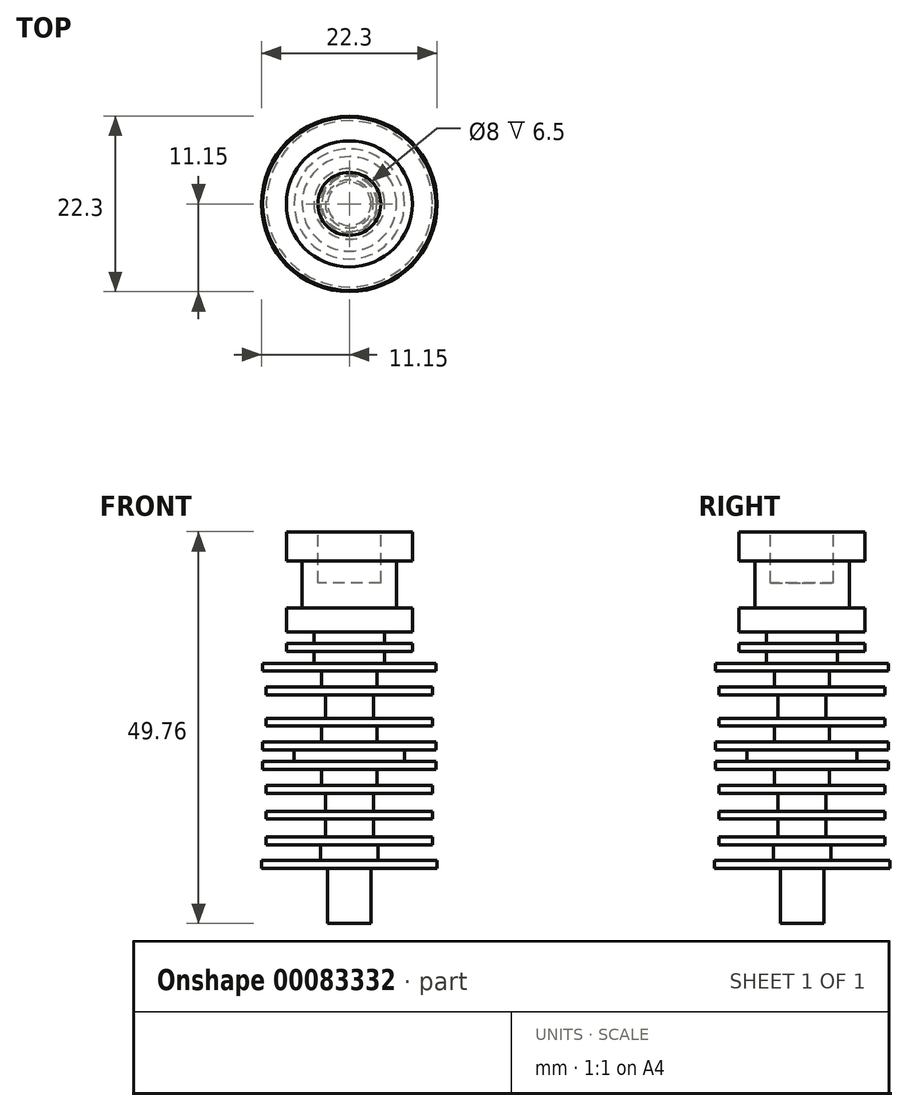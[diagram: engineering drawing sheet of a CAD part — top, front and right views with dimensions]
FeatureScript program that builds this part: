
annotation { "Feature Type Name" : "Feature", "Feature Type Description" : "" }
export const myFeature = defineFeature(function(context is Context, id is Id, definition is map)
    precondition{}
    {
        {
            var Q0;
            Q0=qCreatedBy(makeId("Front.planeOp"),FACE);
            var sketch = newSketch(context, id + "F0", { "sketchPlane" : qUnion([Q0])});
            skLineSegment(sketch, "E0", {"start": v(2.75, 0) * mm, "end": v(11.15, 0) * mm});
            skLineSegment(sketch, "E1", {"start": v(11.15, 0) * mm, "end": v(11.15, 1) * mm});
            skLineSegment(sketch, "E2", {"start": v(11.15, 1) * mm, "end": v(3.65, 1) * mm});
            skLineSegment(sketch, "E3", {"start": v(3.65, 1) * mm, "end": v(3.65, 3) * mm});
            skLineSegment(sketch, "E4", {"start": v(3.65, 3) * mm, "end": v(10.55, 3) * mm});
            skLineSegment(sketch, "E5", {"start": v(10.55, 3) * mm, "end": v(10.55, 4) * mm});
            skLineSegment(sketch, "E6", {"start": v(10.55, 4) * mm, "end": v(3.05, 4) * mm});
            skLineSegment(sketch, "E7", {"start": v(3.05, 4) * mm, "end": v(3.05, 6.25) * mm});
            skLineSegment(sketch, "E8", {"start": v(3.05, 6.25) * mm, "end": v(10.55, 6.25) * mm});
            skLineSegment(sketch, "E9", {"start": v(10.55, 6.25) * mm, "end": v(10.55, 7.25) * mm});
            skLineSegment(sketch, "E10", {"start": v(10.55, 7.25) * mm, "end": v(3.05, 7.25) * mm});
            skLineSegment(sketch, "E11", {"start": v(3.05, 7.25) * mm, "end": v(3.05, 9.5) * mm});
            skLineSegment(sketch, "E12", {"start": v(3.05, 9.5) * mm, "end": v(10.55, 9.5) * mm});
            skLineSegment(sketch, "E13", {"start": v(10.55, 9.5) * mm, "end": v(10.55, 10.56) * mm});
            skLineSegment(sketch, "E14", {"start": v(10.55, 10.56) * mm, "end": v(3.5, 10.56) * mm});
            skLineSegment(sketch, "E15", {"start": v(3.5, 10.56) * mm, "end": v(3.5, 12.56) * mm});
            skLineSegment(sketch, "E16", {"start": v(3.5, 12.56) * mm, "end": v(11, 12.56) * mm});
            skLineSegment(sketch, "E17", {"start": v(11, 12.56) * mm, "end": v(11, 13.56) * mm});
            skLineSegment(sketch, "E18", {"start": v(11, 13.56) * mm, "end": v(7, 13.56) * mm});
            skLineSegment(sketch, "E19", {"start": v(7, 13.56) * mm, "end": v(7, 15.06) * mm});
            skLineSegment(sketch, "E20", {"start": v(7, 15.06) * mm, "end": v(11, 15.06) * mm});
            skLineSegment(sketch, "E21", {"start": v(11, 15.06) * mm, "end": v(11, 16.06) * mm});
            skLineSegment(sketch, "E22", {"start": v(11, 16.06) * mm, "end": v(3.5, 16.06) * mm});
            skLineSegment(sketch, "E23", {"start": v(3.5, 16.06) * mm, "end": v(3.5, 18.06) * mm});
            skLineSegment(sketch, "E24", {"start": v(3.5, 18.06) * mm, "end": v(10.55, 18.06) * mm});
            skLineSegment(sketch, "E25", {"start": v(10.55, 18.06) * mm, "end": v(10.55, 19.06) * mm});
            skLineSegment(sketch, "E26", {"start": v(10.55, 19.06) * mm, "end": v(3.05, 19.06) * mm});
            skLineSegment(sketch, "E27", {"start": v(3.05, 19.06) * mm, "end": v(3.05, 22.06) * mm});
            skLineSegment(sketch, "E28", {"start": v(3.05, 22.06) * mm, "end": v(10.55, 22.06) * mm});
            skLineSegment(sketch, "E29", {"start": v(10.55, 22.06) * mm, "end": v(10.55, 23.06) * mm});
            skLineSegment(sketch, "E30", {"start": v(10.55, 23.06) * mm, "end": v(3.5, 23.06) * mm});
            skLineSegment(sketch, "E31", {"start": v(3.5, 23.06) * mm, "end": v(3.5, 25.06) * mm});
            skLineSegment(sketch, "E32", {"start": v(3.5, 25.06) * mm, "end": v(11, 25.06) * mm});
            skLineSegment(sketch, "E33", {"start": v(11, 25.06) * mm, "end": v(11, 26.06) * mm});
            skLineSegment(sketch, "E34", {"start": v(11, 26.06) * mm, "end": v(4.5, 26.06) * mm});
            skLineSegment(sketch, "E35", {"start": v(4.5, 26.06) * mm, "end": v(4.5, 27.56) * mm});
            skLineSegment(sketch, "E36", {"start": v(4.5, 27.56) * mm, "end": v(8, 27.56) * mm});
            skLineSegment(sketch, "E37", {"start": v(8, 27.56) * mm, "end": v(8, 28.56) * mm});
            skLineSegment(sketch, "E38", {"start": v(8, 28.56) * mm, "end": v(4.5, 28.56) * mm});
            skLineSegment(sketch, "E39", {"start": v(4.5, 28.56) * mm, "end": v(4.5, 30.06) * mm});
            skLineSegment(sketch, "E40", {"start": v(4.5, 30.06) * mm, "end": v(8, 30.06) * mm});
            skLineSegment(sketch, "E41", {"start": v(8, 30.06) * mm, "end": v(8, 33.06) * mm});
            skLineSegment(sketch, "E42", {"start": v(8, 33.06) * mm, "end": v(6, 33.06) * mm});
            skLineSegment(sketch, "E43", {"start": v(6, 33.06) * mm, "end": v(6, 39.06) * mm});
            skLineSegment(sketch, "E44", {"start": v(6, 39.06) * mm, "end": v(8, 39.06) * mm});
            skLineSegment(sketch, "E45", {"start": v(8, 39.06) * mm, "end": v(8, 42.76) * mm});
            skLineSegment(sketch, "E46", {"start": v(8, 42.76) * mm, "end": v(0, 42.76) * mm});
            skLineSegment(sketch, "E47", {"start": v(0, 42.76) * mm, "end": v(0, 0) * mm});
            skLineSegment(sketch, "E48", {"start": v(2.75, 0) * mm, "end": v(2.75, -7) * mm});
            skLineSegment(sketch, "E49", {"start": v(0, -7) * mm, "end": v(0, 0) * mm});
            skLineSegment(sketch, "E50", {"start": v(2.75, -7) * mm, "end": v(0, -7) * mm});
            skSolve(sketch);
        }
        {
            var Q0;
            Q0=makeQuery(id+"F0.imprint","IMPRINT",FACE,{"disambiguationData":[TD([[makeQuery(id+"F0.imprint","IMPRINT",EDGE,{"derivedFrom":sQuery(id+"F0.wireOp",EDGE,"E0")}),1.0]])]});
            var Q1;
            Q1=sQuery(id+"F0.wireOp",EDGE,"E47");
            revolve(context, id + "F1", {"entities" : qUnion([Q0]), "axis" : qUnion([Q1]), "revolveType" : RevolveType.FULL});
        }
        {
            var Q0;
            Q0=makeQuery(id+"F1.opRevolve","SWEPT_FACE",FACE,{"disambiguationData":[OSD([sQuery(id+"F0.wireOp",EDGE,"E46")])]});
            var sketch = newSketch(context, id + "F2", { "sketchPlane" : qUnion([Q0])});
            skCircle(sketch, "E51", {"center": v(0, 0) * mm, "radius": 4 * mm});
            skSolve(sketch);
        }
        {
            var Q0;
            Q0=qSketchRegion(id+"F2",true);
            extrude(context, id + "F3", {"entities" : qUnion([Q0]), "operationType" : NewBodyOperationType.REMOVE, "oppositeDirection" : true, "depth" : 6.5 * mm});
        }
    });
